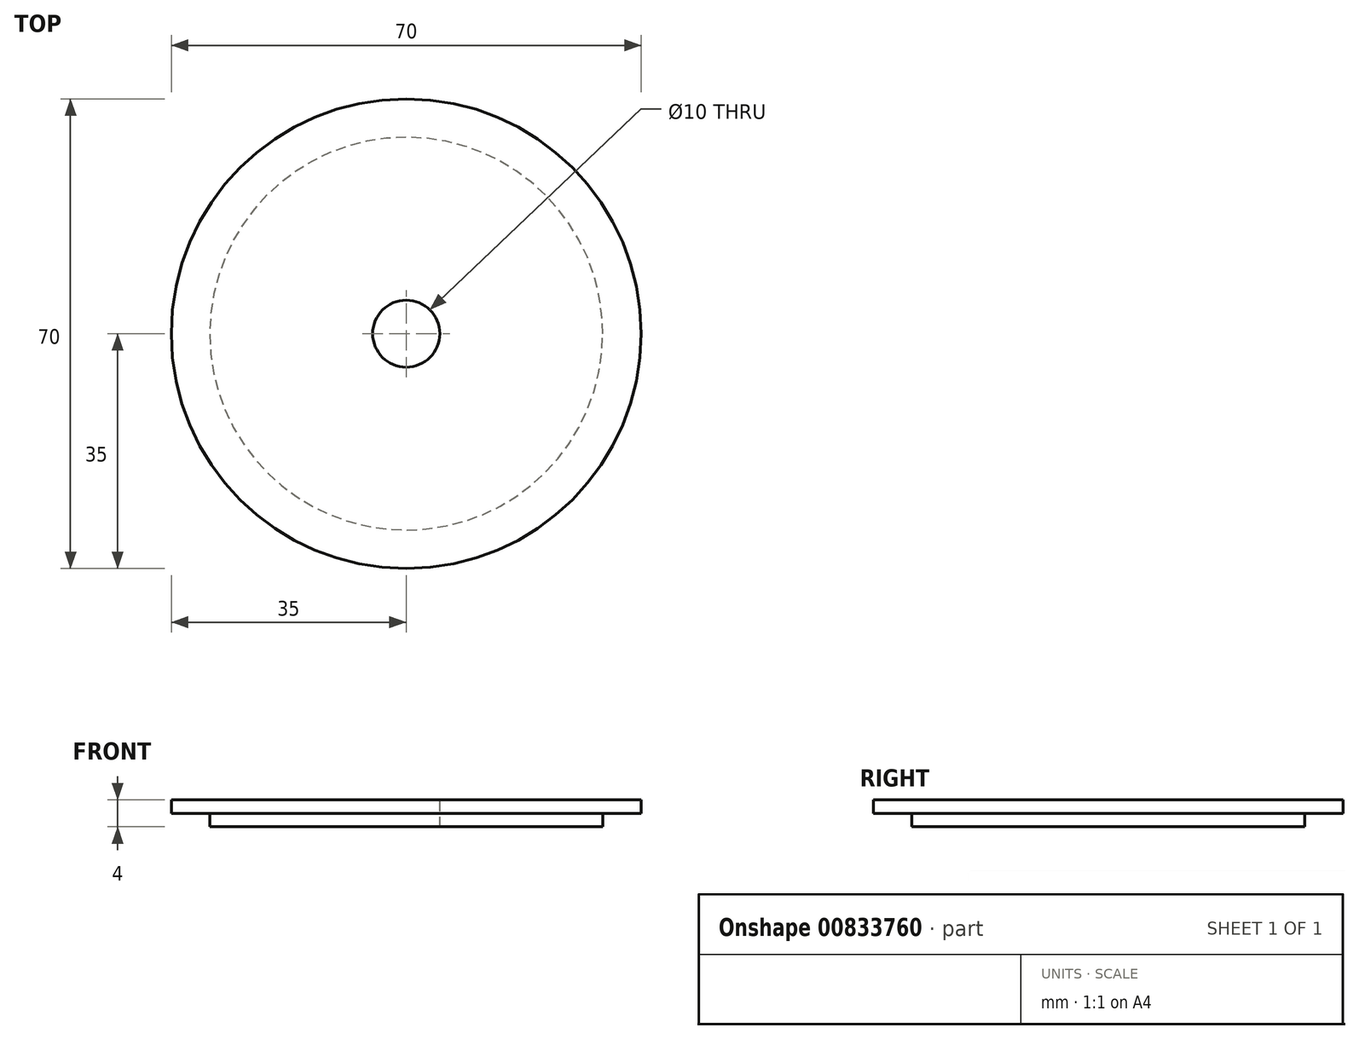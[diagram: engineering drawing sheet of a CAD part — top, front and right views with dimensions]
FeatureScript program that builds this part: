
annotation { "Feature Type Name" : "Feature", "Feature Type Description" : "" }
export const myFeature = defineFeature(function(context is Context, id is Id, definition is map)
    precondition{}
    {
        {
            var Q0;
            Q0=qCreatedBy(makeId("Top.planeOp"),FACE);
            var sketch = newSketch(context, id + "F0", { "sketchPlane" : qUnion([Q0])});
            skCircle(sketch, "E0", {"center": v(0, 0) * mm, "radius": 35 * mm});
            skSolve(sketch);
        }
        {
            var Q0;
            Q0 = qSketchRegion(id + "F0", true);
            extrude(context, id + "F1", {"entities" : qUnion([Q0]), "depth" : 2 * mm, "offsetDistance" : 25 * mm});
        }
        {
            var Q0;
            Q0=makeQuery(id+"F1.opExtrude","CAP_FACE",FACE,{"disambiguationData":[OSD([sQuery(id+"F0.wireOp",EDGE,"E0")])],"isStart":true});
            var sketch = newSketch(context, id + "F2", { "sketchPlane" : qUnion([Q0])});
            skCircle(sketch, "E1", {"center": v(0, 0) * mm, "radius": 29.27 * mm});
            skSolve(sketch);
        }
        {
            var Q0;
            Q0 = qSketchRegion(id + "F2", true);
            extrude(context, id + "F3", {"entities" : qUnion([Q0]), "operationType" : NewBodyOperationType.ADD, "depth" : 2 * mm, "offsetDistance" : 25 * mm});
        }
        {
            var Q0;
            Q0=makeQuery(id+"F1.opExtrude","CAP_FACE",FACE,{"disambiguationData":[OSD([sQuery(id+"F0.wireOp",EDGE,"E0")])],"isStart":false});
            var sketch = newSketch(context, id + "F4", { "sketchPlane" : qUnion([Q0])});
            skCircle(sketch, "E2", {"center": v(0, 0) * mm, "radius": 5 * mm});
            skSolve(sketch);
        }
        {
            var Q0;
            Q0 = qSketchRegion(id + "F4", true);
            extrude(context, id + "F5", {"entities" : qUnion([Q0]), "operationType" : NewBodyOperationType.REMOVE, "endBound" : BoundingType.UP_TO_NEXT, "oppositeDirection" : true, "depth" : 25 * mm, "offsetDistance" : 25 * mm});
        }
    });
